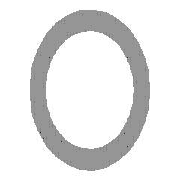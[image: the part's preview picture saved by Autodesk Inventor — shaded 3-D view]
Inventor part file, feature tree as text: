
AUTODESK INVENTOR PART (.ipt)
format: ipt  version: 2021 (Build 250183000, 183)  size: 380,416 bytes
history: native  units: mm (DEFAULTED — no unit token found)
features: other x14, plane x4, sketch x4, sweep x1, split x1, loft x1
ambient origin geometry x8: Origin, YZ Plane, XZ Plane, XY Plane, X Axis, Y Axis, Z Axis, Center Point
bodies: Solid1 (feature_tree)
feature tree (25):
  parser-record x1  (decoder bookkeeping rows leaked as tree rows — omitted from the tree; the rows remain in map.json)
  other  "Driven Length"
  other  "Plano inicial"
  other  "Plano final"
  other  "Trayectoria de barrido"
  plane  "Plano de trabajo de orientación"
  sweep  "Cuerpo"
  plane  "Plano de trabajo8"
  split  "Dividir4"
  plane  "Plano de trabajo9"
  loft  "Solevación1"
  sketch  "Sketch3"  dims[d0=26.67mm d1=2.8702mm]
  plane  "Work Plane3"
  sketch  "Sketch4"  dims[d4=-0.0mm d5=505.770567mm]
  sketch  "Boceto8"  dims[d6=90.0deg]
  other  "Sup148"
  other  "Sup150"
  other  "Sup151"
  other  "Sólido50"
  sketch  "Boceto9"  dims[d7=505.770567mm d8=0.0mm d9=0.0mm d26=10.0mm d31=10.0mm d216=0.0mm d217=90.0deg d218=0.0mm d219=90.0deg d220=5.0mm d221=0.0mm d222=5.0mm d223=0.0mm d224=7.0mm d225=10.0mm d226=25.0mm d227=0.0mm d228=90.0deg d229=0.0mm d230=90.0deg d231=2.0mm d232=20.0mm d233=5.0mm]
  other  "Aristas1"
  other  "SuperficieSolevación4"
  other  "Sup149"
  other  "Superficie de contorno97"
  other  "Superficie de contorno98"
